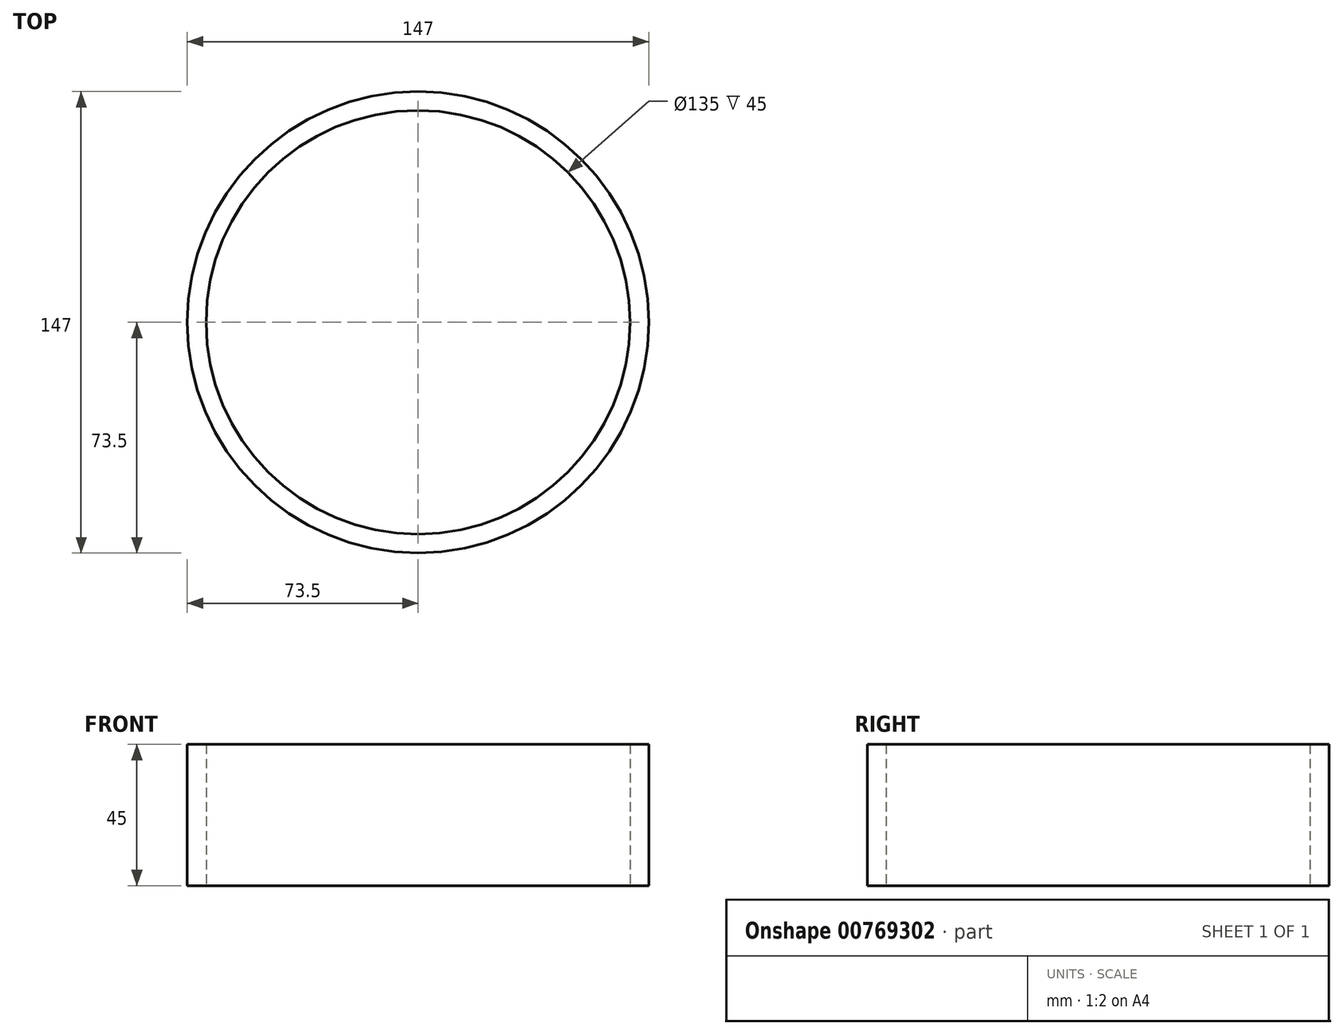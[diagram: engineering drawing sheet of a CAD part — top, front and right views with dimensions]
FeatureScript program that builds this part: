
annotation { "Feature Type Name" : "Feature", "Feature Type Description" : "" }
export const myFeature = defineFeature(function(context is Context, id is Id, definition is map)
    precondition{}
    {
        {
            var Q0;
            Q0=qCreatedBy(makeId("Top.planeOp"),FACE);
            var sketch = newSketch(context, id + "F0", { "sketchPlane" : qUnion([Q0])});
            skCircle(sketch, "E0", {"center": v(0, 0) * mm, "radius": 50 * mm});
            skCircle(sketch, "E1", {"center": v(0, 0) * mm, "radius": 67.5 * mm});
            skCircle(sketch, "E2", {"center": v(0, 0) * mm, "radius": 70.5 * mm});
            skCircle(sketch, "E3", {"center": v(0, 0) * mm, "radius": 73.5 * mm});
            skCircle(sketch, "E4", {"center": v(0, 0) * mm, "radius": 56.9 * mm, "construction": true});
            skPoint(sketch, "E5", {"position": v(56.9, 0) * mm});
            skPoint(sketch, "E6", {"position": v(67.5, 0) * mm});
            skPoint(sketch, "E7", {"position": v(70.5, 0) * mm});
            skPoint(sketch, "E8", {"position": v(73.5, 0) * mm});
            skLineSegment(sketch, "E9", {"start": v(0, 0) * mm, "end": v(0, 56.9) * mm, "construction": true});
            skLineSegment(sketch, "E10", {"start": v(0, 0) * mm, "end": v(-49.28, -28.45) * mm, "construction": true});
            skLineSegment(sketch, "E11", {"start": v(0, 0) * mm, "end": v(49.28, -28.45) * mm, "construction": true});
            skPoint(sketch, "E12", {"position": v(0, 56.9) * mm});
            skPoint(sketch, "E13", {"position": v(-49.28, -28.45) * mm});
            skPoint(sketch, "E14", {"position": v(49.28, -28.45) * mm});
            skPoint(sketch, "E15", {"position": v(0, 73.5) * mm});
            skLineSegment(sketch, "E16", {"start": v(-49.28, -28.45) * mm, "end": v(-63.47, -37.07) * mm, "construction": true});
            skPoint(sketch, "E17", {"position": v(-63.47, -37.07) * mm});
            skLineSegment(sketch, "E18", {"start": v(49.28, -28.45) * mm, "end": v(63.65, -36.75) * mm, "construction": true});
            skPoint(sketch, "E19", {"position": v(63.65, -36.75) * mm});
            skSolve(sketch);
        }
        {
            var Q0;
            Q0=qCreatedBy(makeId("Front.planeOp"),FACE);
            cPlane(context, id + "F1", {"entities" : qUnion([Q0]), "cplaneType" : CPlaneType.OFFSET, "offset" : 75 * mm, "width" : 150 * mm, "height" : 150 * mm});
        }
        {
            var Q0;
            Q0=qCreatedBy(id+"F1.planeOp",FACE);
            var sketch = newSketch(context, id + "F2", { "sketchPlane" : qUnion([Q0])});
            skPoint(sketch, "E20", {"position": v(433.27, 100.43) * mm});
            skPoint(sketch, "E21", {"position": v(0, 0) * mm});
            skSolve(sketch);
        }
        {
            var Q0;
            Q0 = qSketchRegion(id + "F2", true);
            var Q1;
            Q1=makeQuery(id+"F0.imprint","IMPRINT",FACE,{"disambiguationData":[TD([[makeQuery(id+"F0.imprint","IMPRINT",EDGE,{"derivedFrom":sQuery(id+"F0.wireOp",EDGE,"E2")}),-1.0]])]});
            var Q2;
            Q2=makeQuery(id+"F0.imprint","IMPRINT",FACE,{"disambiguationData":[TD([[makeQuery(id+"F0.imprint","IMPRINT",EDGE,{"derivedFrom":sQuery(id+"F0.wireOp",EDGE,"E1")}),-1.0]])]});
            extrude(context, id + "F3", {"entities" : qUnion([Q0, Q1, Q2]), "depth" : 45 * mm, "offsetDistance" : 25 * mm});
        }
        {
            var Q0;
            Q0=qCreatedBy(makeId("Top.planeOp"),FACE);
            cPlane(context, id + "F4", {"entities" : qUnion([Q0]), "cplaneType" : CPlaneType.OFFSET, "offset" : 45 * mm, "width" : 150 * mm, "height" : 150 * mm});
        }
        {
            var Q0;
            Q0=qCreatedBy(id+"F4.planeOp",FACE);
            cPlane(context, id + "F5", {"entities" : qUnion([Q0]), "cplaneType" : CPlaneType.OFFSET, "offset" : 15 * mm, "width" : 150 * mm, "height" : 150 * mm});
        }
    });
